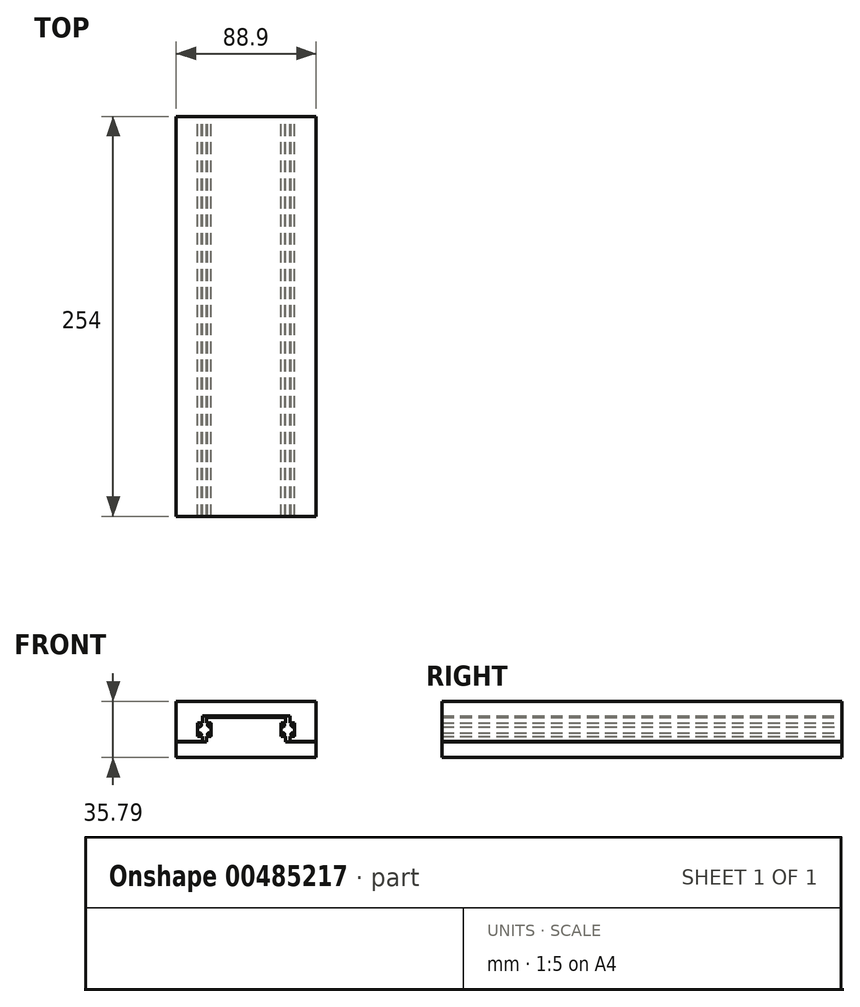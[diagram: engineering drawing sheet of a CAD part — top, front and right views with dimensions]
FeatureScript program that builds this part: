
annotation { "Feature Type Name" : "Feature", "Feature Type Description" : "" }
export const myFeature = defineFeature(function(context is Context, id is Id, definition is map)
    precondition{}
    {
        {
            var Q0;
            Q0=qCreatedBy(makeId("Front.planeOp"),FACE);
            var sketch = newSketch(context, id + "F0", { "sketchPlane" : qUnion([Q0])});
            skLineSegment(sketch, "E0.bottom", {"start": v(44.45, -12.7) * mm, "end": v(-44.45, -12.7) * mm});
            skLineSegment(sketch, "E0.top", {"start": v(25.15, 12.7) * mm, "end": v(-25.15, 12.7) * mm});
            skLineSegment(sketch, "E0.left", {"start": v(44.45, -12.7) * mm, "end": v(44.45, -2.8) * mm});
            skLineSegment(sketch, "E0.right", {"start": v(-44.45, -12.7) * mm, "end": v(-44.45, -2.8) * mm});
            skPoint(sketch, "E0.middle", {"position": v(0, 0) * mm});
            skLineSegment(sketch, "E1", {"start": v(-44.45, -2.8) * mm, "end": v(-25.15, -2.8) * mm});
            skLineSegment(sketch, "E2", {"start": v(-25.15, 12.7) * mm, "end": v(-25.15, 9.17) * mm});
            skPoint(sketch, "E3.orphan", {"position": v(-44.45, 12.7) * mm});
            skPoint(sketch, "E4.orphan", {"position": v(44.45, 12.7) * mm});
            skLineSegment(sketch, "E5.trimOffspring", {"start": v(25.15, -2.8) * mm, "end": v(44.45, -2.8) * mm});
            skLineSegment(sketch, "E6", {"start": v(0, 0) * mm, "end": v(0, 36.5) * mm, "construction": true});
            skPoint(sketch, "E6.endSnap0", {"position": v(0, 12.7) * mm});
            skLineSegment(sketch, "E7", {"start": v(-25.15, 9.17) * mm, "end": v(-22.17, 9.17) * mm});
            skLineSegment(sketch, "E8", {"start": v(-22.17, 9.17) * mm, "end": v(-22.17, 0.74) * mm});
            skLineSegment(sketch, "E9", {"start": v(-22.17, 0.74) * mm, "end": v(-25.15, 0.74) * mm});
            skLineSegment(sketch, "E10.MirrorCS", {"start": v(25.15, 9.17) * mm, "end": v(22.17, 9.17) * mm});
            skLineSegment(sketch, "E11.MirrorCS", {"start": v(22.17, 9.17) * mm, "end": v(22.17, 0.74) * mm});
            skLineSegment(sketch, "E12.MirrorCS", {"start": v(22.17, 0.74) * mm, "end": v(25.15, 0.74) * mm});
            skLineSegment(sketch, "E13.trimOffspring", {"start": v(-25.15, 0.74) * mm, "end": v(-25.15, -2.8) * mm});
            skLineSegment(sketch, "E14", {"start": v(25.15, 12.7) * mm, "end": v(25.15, 9.17) * mm});
            skLineSegment(sketch, "E15", {"start": v(25.15, 0.74) * mm, "end": v(25.15, -2.8) * mm});
            skLineSegment(sketch, "E16.bottom", {"start": v(-27.81, -2.31) * mm, "end": v(27.81, -2.31) * mm, "construction": true});
            skLineSegment(sketch, "E16.top", {"start": v(-27.81, 13.8) * mm, "end": v(27.81, 13.8) * mm});
            skLineSegment(sketch, "E16.left", {"start": v(-27.81, -2.31) * mm, "end": v(-27.81, 0.74) * mm});
            skLineSegment(sketch, "E16.right", {"start": v(27.81, -2.31) * mm, "end": v(27.81, 0.74) * mm});
            skLineSegment(sketch, "E17", {"start": v(-27.81, -2.31) * mm, "end": v(-44.45, -2.31) * mm});
            skLineSegment(sketch, "E18", {"start": v(-44.45, -2.31) * mm, "end": v(-44.45, 23.09) * mm});
            skLineSegment(sketch, "E19", {"start": v(-44.45, 23.09) * mm, "end": v(44.45, 23.09) * mm});
            skLineSegment(sketch, "E20", {"start": v(44.45, 23.09) * mm, "end": v(44.45, -2.31) * mm});
            skLineSegment(sketch, "E21", {"start": v(44.45, -2.31) * mm, "end": v(27.81, -2.31) * mm});
            skLineSegment(sketch, "E22", {"start": v(-27.81, 9.17) * mm, "end": v(-30.78, 9.17) * mm});
            skLineSegment(sketch, "E23", {"start": v(-30.78, 9.17) * mm, "end": v(-30.78, 0.74) * mm});
            skLineSegment(sketch, "E24", {"start": v(-30.78, 0.74) * mm, "end": v(-27.81, 0.74) * mm});
            skLineSegment(sketch, "E25.trimOffspring", {"start": v(-27.81, 9.17) * mm, "end": v(-27.81, 13.8) * mm});
            skCircle(sketch, "E26", {"center": v(-29.6, 7.99) * mm, "radius": 1.18 * mm});
            skCircle(sketch, "E27", {"center": v(-23.36, 7.99) * mm, "radius": 1.18 * mm});
            skCircle(sketch, "E28", {"center": v(-29.6, 1.92) * mm, "radius": 1.18 * mm});
            skCircle(sketch, "E29", {"center": v(-23.36, 1.92) * mm, "radius": 1.18 * mm});
            skCircle(sketch, "E30", {"center": v(-26.48, 4.95) * mm, "radius": 3.17 * mm});
            skLineSegment(sketch, "E31", {"start": v(27.81, 9.17) * mm, "end": v(30.78, 9.17) * mm});
            skLineSegment(sketch, "E32", {"start": v(30.78, 9.17) * mm, "end": v(30.78, 0.74) * mm});
            skLineSegment(sketch, "E33", {"start": v(30.78, 0.74) * mm, "end": v(27.81, 0.74) * mm});
            skLineSegment(sketch, "E34.trimOffspring", {"start": v(27.81, 9.17) * mm, "end": v(27.81, 13.8) * mm});
            skCircle(sketch, "E35", {"center": v(23.36, 7.99) * mm, "radius": 1.18 * mm});
            skCircle(sketch, "E36", {"center": v(29.6, 7.99) * mm, "radius": 1.18 * mm});
            skCircle(sketch, "E37", {"center": v(23.36, 1.92) * mm, "radius": 1.18 * mm});
            skCircle(sketch, "E38", {"center": v(29.6, 1.92) * mm, "radius": 1.18 * mm});
            skCircle(sketch, "E39", {"center": v(26.48, 4.95) * mm, "radius": 3.17 * mm});
            skSolve(sketch);
        }
        {
            var Q0;
            Q0=makeQuery(id+"F0.imprint","IMPRINT",FACE,{"disambiguationData":[TD([[makeQuery(id+"F0.imprint","IMPRINT",EDGE,{"derivedFrom":sQuery(id+"F0.wireOp",EDGE,"E0.bottom")}),-1.0]])]});
            extrude(context, id + "F1", {"entities" : qUnion([Q0]), "depth" : 254 * mm, "offsetDistance" : 25.4 * mm});
        }
        {
            var Q0;
            Q0=makeQuery(id+"F0.imprint","IMPRINT",FACE,{"disambiguationData":[TD([[makeQuery(id+"F0.imprint","IMPRINT",EDGE,{"derivedFrom":sQuery(id+"F0.wireOp",EDGE,"E16.top")}),1.0]])]});
            extrude(context, id + "F2", {"entities" : qUnion([Q0]), "depth" : 254 * mm, "offsetDistance" : 25.4 * mm});
        }
        {
            var Q0;
            {var subQ0=sQuery(id+"F0.wireOp",EDGE,"E26");var subQ1=makeQuery(id+"F0.imprint","INTERSECT",VERTEX,{"derivedFrom":[sQuery(id+"F0.wireOp",EDGE,"E22"),subQ0]});Q0=makeQuery(id+"F0.imprint","IMPRINT",FACE,{"disambiguationData":[TD([[makeQuery(id+"F0.imprint","IMPRINT",EDGE,{"disambiguationData":[TD([[subQ1,-1.0]])],"derivedFrom":subQ0}),1.0]])]});}
            var Q1;
            {var subQ0=sQuery(id+"F0.wireOp",EDGE,"E28");var subQ1=makeQuery(id+"F0.imprint","INTERSECT",VERTEX,{"derivedFrom":[subQ0,sQuery(id+"F0.wireOp",EDGE,"E30")]});Q1=makeQuery(id+"F0.imprint","IMPRINT",FACE,{"disambiguationData":[TD([[makeQuery(id+"F0.imprint","IMPRINT",EDGE,{"disambiguationData":[TD([[subQ1,-1.0]])],"derivedFrom":subQ0}),1.0]])]});}
            var Q2;
            {var subQ0=sQuery(id+"F0.wireOp",EDGE,"E27");var subQ1=makeQuery(id+"F0.imprint","INTERSECT",VERTEX,{"derivedFrom":[sQuery(id+"F0.wireOp",EDGE,"E7"),subQ0]});Q2=makeQuery(id+"F0.imprint","IMPRINT",FACE,{"disambiguationData":[TD([[makeQuery(id+"F0.imprint","IMPRINT",EDGE,{"disambiguationData":[TD([[subQ1,1.0]])],"derivedFrom":subQ0}),1.0]])]});}
            var Q3;
            {var subQ0=sQuery(id+"F0.wireOp",EDGE,"E29");var subQ1=makeQuery(id+"F0.imprint","INTERSECT",VERTEX,{"derivedFrom":[subQ0,sQuery(id+"F0.wireOp",EDGE,"E30")]});Q3=makeQuery(id+"F0.imprint","IMPRINT",FACE,{"disambiguationData":[TD([[makeQuery(id+"F0.imprint","IMPRINT",EDGE,{"disambiguationData":[TD([[subQ1,1.0]])],"derivedFrom":subQ0}),1.0]])]});}
            extrude(context, id + "F3", {"entities" : qUnion([Q0, Q1, Q2, Q3]), "depth" : 254 * mm, "offsetDistance" : 25.4 * mm});
        }
        {
            var Q0;
            {var subQ0=sQuery(id+"F0.wireOp",EDGE,"E35");var subQ1=makeQuery(id+"F0.imprint","INTERSECT",VERTEX,{"derivedFrom":[sQuery(id+"F0.wireOp",EDGE,"E10.MirrorCS"),subQ0]});Q0=makeQuery(id+"F0.imprint","IMPRINT",FACE,{"disambiguationData":[TD([[makeQuery(id+"F0.imprint","IMPRINT",EDGE,{"disambiguationData":[TD([[subQ1,-1.0]])],"derivedFrom":subQ0}),1.0]])]});}
            var Q1;
            {var subQ0=sQuery(id+"F0.wireOp",EDGE,"E36");var subQ1=makeQuery(id+"F0.imprint","INTERSECT",VERTEX,{"derivedFrom":[sQuery(id+"F0.wireOp",EDGE,"E31"),subQ0]});Q1=makeQuery(id+"F0.imprint","IMPRINT",FACE,{"disambiguationData":[TD([[makeQuery(id+"F0.imprint","IMPRINT",EDGE,{"disambiguationData":[TD([[subQ1,1.0]])],"derivedFrom":subQ0}),1.0]])]});}
            var Q2;
            {var subQ0=sQuery(id+"F0.wireOp",EDGE,"E38");var subQ1=makeQuery(id+"F0.imprint","INTERSECT",VERTEX,{"derivedFrom":[subQ0,sQuery(id+"F0.wireOp",EDGE,"E39")]});Q2=makeQuery(id+"F0.imprint","IMPRINT",FACE,{"disambiguationData":[TD([[makeQuery(id+"F0.imprint","IMPRINT",EDGE,{"disambiguationData":[TD([[subQ1,1.0]])],"derivedFrom":subQ0}),1.0]])]});}
            var Q3;
            {var subQ0=sQuery(id+"F0.wireOp",EDGE,"E37");var subQ1=makeQuery(id+"F0.imprint","INTERSECT",VERTEX,{"derivedFrom":[subQ0,sQuery(id+"F0.wireOp",EDGE,"E39")]});Q3=makeQuery(id+"F0.imprint","IMPRINT",FACE,{"disambiguationData":[TD([[makeQuery(id+"F0.imprint","IMPRINT",EDGE,{"disambiguationData":[TD([[subQ1,-1.0]])],"derivedFrom":subQ0}),1.0]])]});}
            extrude(context, id + "F4", {"entities" : qUnion([Q0, Q1, Q2, Q3]), "depth" : 254 * mm, "offsetDistance" : 25.4 * mm});
        }
    });
